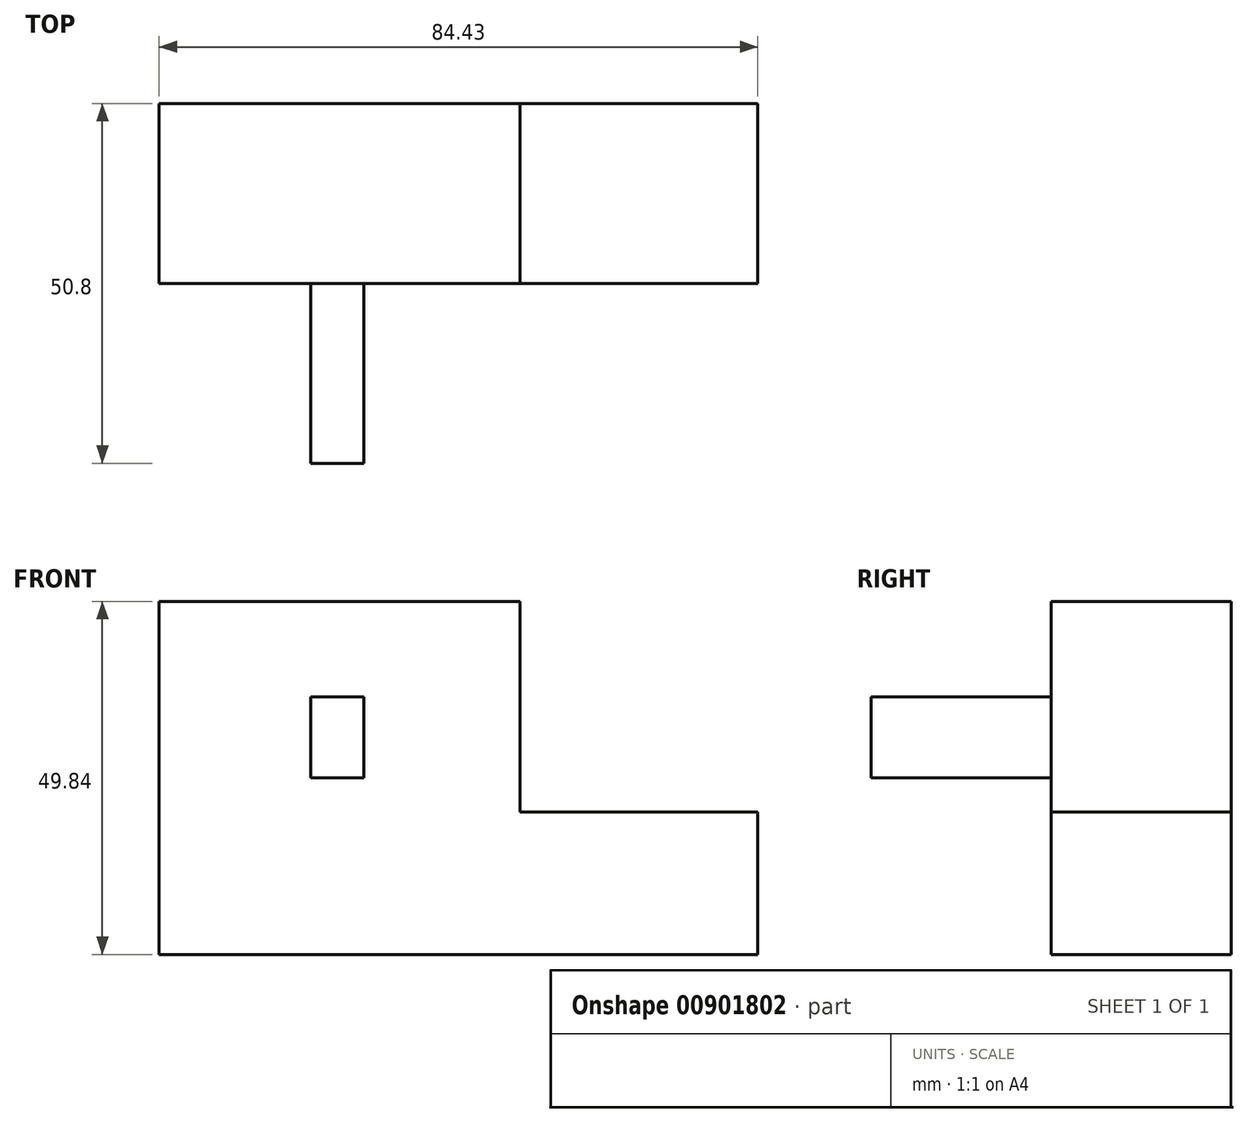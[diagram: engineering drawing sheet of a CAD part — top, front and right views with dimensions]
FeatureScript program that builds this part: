
annotation { "Feature Type Name" : "Feature", "Feature Type Description" : "" }
export const myFeature = defineFeature(function(context is Context, id is Id, definition is map)
    precondition{}
    {
        {
            var Q0;
            Q0=qCreatedBy(makeId("Front.planeOp"),FACE);
            var sketch = newSketch(context, id + "F0", { "sketchPlane" : qUnion([Q0])});
            skLineSegment(sketch, "E0.bottom", {"start": v(50.92, 49.84) * mm, "end": v(0, 49.84) * mm});
            skLineSegment(sketch, "E0.top", {"start": v(50.92, 0) * mm, "end": v(0, 0) * mm});
            skLineSegment(sketch, "E0.left", {"start": v(50.92, 49.84) * mm, "end": v(50.92, 0) * mm});
            skLineSegment(sketch, "E0.right", {"start": v(0, 49.84) * mm, "end": v(0, 0) * mm});
            skLineSegment(sketch, "E1.bottom", {"start": v(50.92, 0) * mm, "end": v(84.43, 0) * mm});
            skLineSegment(sketch, "E1.top", {"start": v(50.92, 20.12) * mm, "end": v(84.43, 20.12) * mm});
            skLineSegment(sketch, "E1.left", {"start": v(50.92, 0) * mm, "end": v(50.92, 20.12) * mm});
            skLineSegment(sketch, "E1.right", {"start": v(84.43, 0) * mm, "end": v(84.43, 20.12) * mm});
            skSolve(sketch);
        }
        {
            var Q0;
            Q0 = qSketchRegion(id + "F0", true);
            extrude(context, id + "F1", {"entities" : qUnion([Q0]), "depth" : 25.4 * mm, "offsetDistance" : 25.4 * mm});
        }
        {
            var Q0;
            Q0=makeQuery(id+"F1.opExtrude","CAP_FACE",FACE,{"disambiguationData":[OSD([sQuery(id+"F0.wireOp",EDGE,"E0.bottom"),sQuery(id+"F0.wireOp",EDGE,"E0.top"),sQuery(id+"F0.wireOp",EDGE,"E0.left"),sQuery(id+"F0.wireOp",EDGE,"E0.right"),sQuery(id+"F0.wireOp",EDGE,"E1.bottom"),sQuery(id+"F0.wireOp",EDGE,"E1.top"),sQuery(id+"F0.wireOp",EDGE,"E1.right")])],"isStart":false});
            var sketch = newSketch(context, id + "F2", { "sketchPlane" : qUnion([Q0])});
            skPoint(sketch, "E2.oppositeSnap0", {"position": v(0, 24.92) * mm});
            skLineSegment(sketch, "E2.bottom", {"start": v(0, 24.92) * mm, "end": v(28.87, 24.92) * mm});
            skLineSegment(sketch, "E2.top", {"start": v(0, 24.92) * mm, "end": v(28.87, 24.92) * mm});
            skLineSegment(sketch, "E2.left", {"start": v(0, 24.92) * mm, "end": v(0, 24.92) * mm});
            skLineSegment(sketch, "E2.right", {"start": v(28.87, 24.92) * mm, "end": v(28.87, 24.92) * mm});
            skLineSegment(sketch, "E3.bottom", {"start": v(21.37, 24.92) * mm, "end": v(28.87, 24.92) * mm});
            skLineSegment(sketch, "E3.top", {"start": v(21.37, 24.92) * mm, "end": v(28.87, 24.92) * mm});
            skLineSegment(sketch, "E3.left", {"start": v(21.37, 24.92) * mm, "end": v(21.37, 24.92) * mm});
            skLineSegment(sketch, "E4.top", {"start": v(21.37, 36.4) * mm, "end": v(28.87, 36.4) * mm});
            skLineSegment(sketch, "E4.left", {"start": v(21.37, 24.92) * mm, "end": v(21.37, 36.4) * mm});
            skLineSegment(sketch, "E4.right", {"start": v(28.87, 24.92) * mm, "end": v(28.87, 36.4) * mm});
            skSolve(sketch);
        }
        {
            var Q0;
            Q0 = qSketchRegion(id + "F2", true);
            extrude(context, id + "F3", {"entities" : qUnion([Q0]), "operationType" : NewBodyOperationType.ADD, "depth" : 25.4 * mm, "offsetDistance" : 25.4 * mm});
        }
    });
